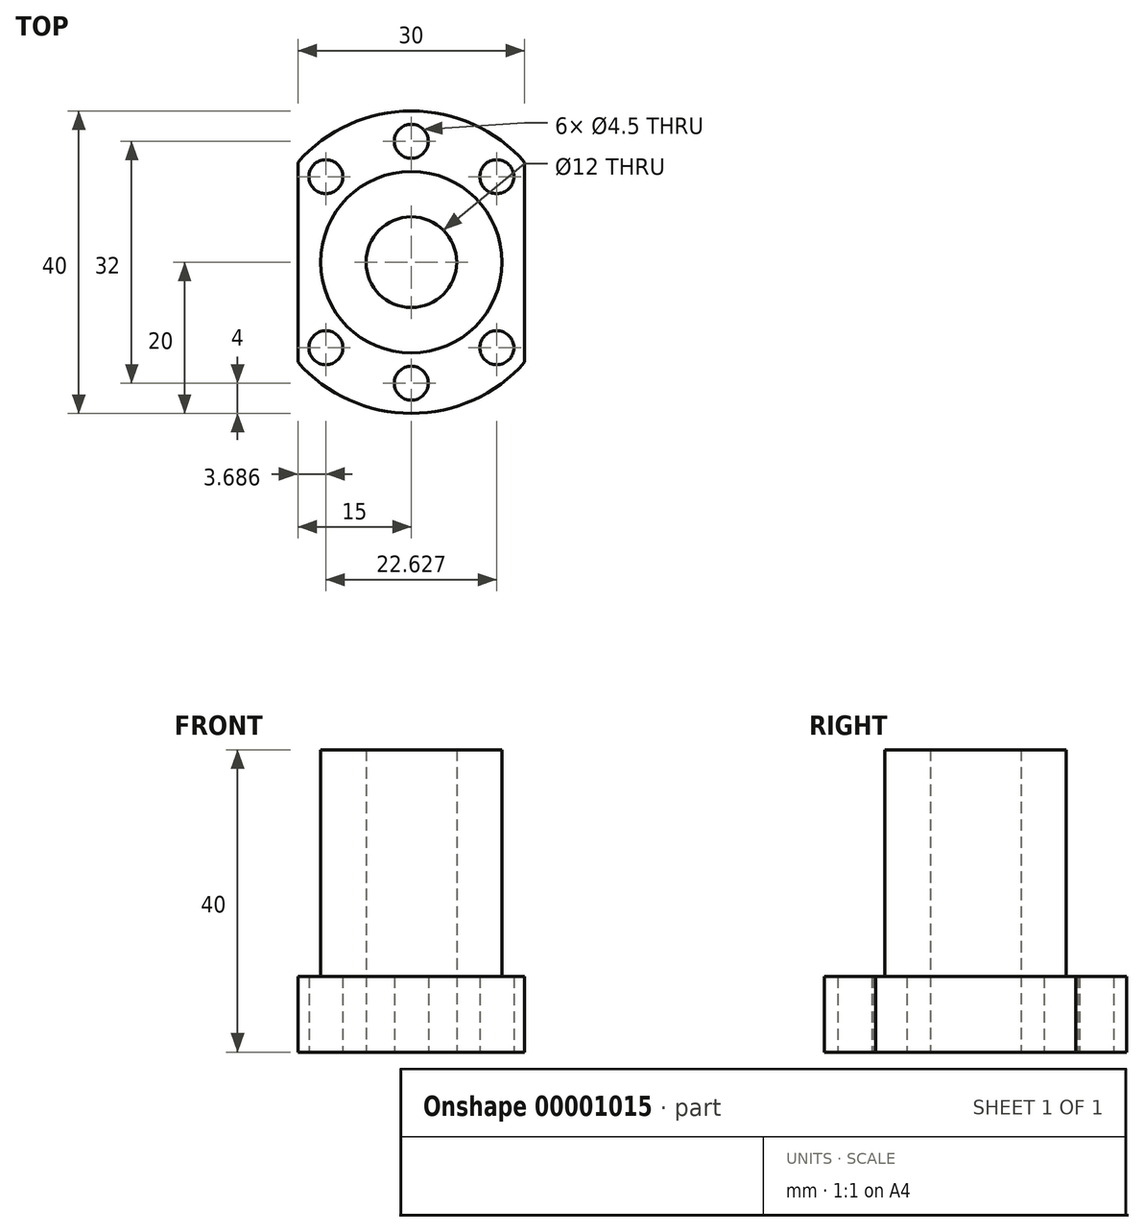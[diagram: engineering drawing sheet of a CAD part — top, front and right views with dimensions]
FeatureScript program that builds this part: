
annotation { "Feature Type Name" : "Feature", "Feature Type Description" : "" }
export const myFeature = defineFeature(function(context is Context, id is Id, definition is map)
    precondition{}
    {
        {
            var Q0;
            Q0=qCreatedBy(makeId("Top.planeOp"),FACE);
            var sketch = newSketch(context, id + "F0", { "sketchPlane" : qUnion([Q0])});
            skArc(sketch, "E0", {"start": v(-15, -13.23) * mm, "mid": v(0, -20) * mm, "end": v(15, -13.23) * mm});
            skLineSegment(sketch, "E1.rect.left", {"start": v(-15, 13.23) * mm, "end": v(-15, -13.23) * mm});
            skLineSegment(sketch, "E1.rect.right", {"start": v(15, 13.23) * mm, "end": v(15, -13.23) * mm});
            skPoint(sketch, "E1.rect.top.start.orphan", {"position": v(-15, -32.41) * mm});
            skPoint(sketch, "E2.orphan", {"position": v(15, -32.41) * mm});
            skArc(sketch, "E3.trimOffspring", {"start": v(15, 13.23) * mm, "mid": v(0, 20) * mm, "end": v(-15, 13.23) * mm});
            skPoint(sketch, "E1.rect.bottom.start.orphan", {"position": v(-15, 32.41) * mm});
            skPoint(sketch, "E4.orphan", {"position": v(15, 32.41) * mm});
            skCircle(sketch, "E5", {"center": v(0, 0) * mm, "radius": 16 * mm, "construction": true});
            skCircle(sketch, "E6", {"center": v(0, 0) * mm, "radius": 6 * mm});
            skCircle(sketch, "E7", {"center": v(0, 16) * mm, "radius": 2.25 * mm});
            skCircle(sketch, "E8", {"center": v(11.31, 11.31) * mm, "radius": 2.25 * mm});
            skCircle(sketch, "E9", {"center": v(-11.31, 11.31) * mm, "radius": 2.25 * mm});
            skLineSegment(sketch, "E10", {"start": v(0, 0) * mm, "end": v(-31.3, 0) * mm, "construction": true});
            skLineSegment(sketch, "E11", {"start": v(0, 0) * mm, "end": v(-29.04, 29.04) * mm, "construction": true});
            skLineSegment(sketch, "E12", {"start": v(0, 0) * mm, "end": v(25.68, 25.68) * mm, "construction": true});
            skCircle(sketch, "E13.0.MirrorC", {"center": v(11.31, -11.31) * mm, "radius": 2.25 * mm});
            skCircle(sketch, "E13.1.MirrorC", {"center": v(0, -16) * mm, "radius": 2.25 * mm});
            skCircle(sketch, "E13.2.MirrorC", {"center": v(-11.31, -11.31) * mm, "radius": 2.25 * mm});
            skSolve(sketch);
        }
        {
            var Q0;
            Q0=makeQuery(id+"F0.imprint","IMPRINT",FACE,{"disambiguationData":[TD([[makeQuery(id+"F0.imprint","IMPRINT",EDGE,{"derivedFrom":sQuery(id+"F0.wireOp",EDGE,"E0")}),1.0]])]});
            extrude(context, id + "F1", {"entities" : qUnion([Q0]), "depth" : 40 * mm});
        }
        {
            var Q0;
            Q0=makeQuery(id+"F1.opExtrude","CAP_FACE",FACE,{"disambiguationData":[OSD([sQuery(id+"F0.wireOp",EDGE,"E0"),sQuery(id+"F0.wireOp",EDGE,"E1.rect.left"),sQuery(id+"F0.wireOp",EDGE,"E1.rect.right"),sQuery(id+"F0.wireOp",EDGE,"E3.trimOffspring"),sQuery(id+"F0.wireOp",EDGE,"E6"),sQuery(id+"F0.wireOp",EDGE,"E7"),sQuery(id+"F0.wireOp",EDGE,"E8"),sQuery(id+"F0.wireOp",EDGE,"E9"),sQuery(id+"F0.wireOp",EDGE,"E13.0.MirrorC"),sQuery(id+"F0.wireOp",EDGE,"E13.1.MirrorC"),sQuery(id+"F0.wireOp",EDGE,"E13.2.MirrorC")])],"isStart":false});
            var sketch = newSketch(context, id + "F2", { "sketchPlane" : qUnion([Q0])});
            skCircle(sketch, "E14", {"center": v(0, 0) * mm, "radius": 12 * mm});
            skCircle(sketch, "E15", {"center": v(0, 0) * mm, "radius": 27.62 * mm});
            skSolve(sketch);
        }
        {
            var Q0;
            Q0=makeQuery(id+"F2.imprint","IMPRINT",FACE,{"disambiguationData":[TD([[makeQuery(id+"F2.imprint","IMPRINT",EDGE,{"derivedFrom":sQuery(id+"F2.wireOp",EDGE,"E15")}),1.0]])]});
            var Q1;
            Q1=makeQuery(id+"F2.imprint","IMPRINT",FACE,{"disambiguationData":[TD([[makeQuery(id+"F2.imprint","IMPRINT",EDGE,{"derivedFrom":makeQuery(id+"F1.opExtrude","CAP_EDGE",EDGE,{"disambiguationData":[OSD([sQuery(id+"F0.wireOp",EDGE,"E6")])],"isStart":false})}),1.0]])]});
            var Q2;
            Q2=makeQuery(id+"F2.imprint","IMPRINT",FACE,{"disambiguationData":[TD([[makeQuery(id+"F2.imprint","IMPRINT",EDGE,{"derivedFrom":makeQuery(id+"F1.opExtrude","CAP_EDGE",EDGE,{"disambiguationData":[OSD([sQuery(id+"F0.wireOp",EDGE,"E7")])],"isStart":false})}),1.0]])]});
            var Q3;
            Q3=makeQuery(id+"F2.imprint","IMPRINT",FACE,{"disambiguationData":[TD([[makeQuery(id+"F2.imprint","IMPRINT",EDGE,{"derivedFrom":makeQuery(id+"F1.opExtrude","CAP_EDGE",EDGE,{"disambiguationData":[OSD([sQuery(id+"F0.wireOp",EDGE,"E8")])],"isStart":false})}),1.0]])]});
            var Q4;
            Q4=makeQuery(id+"F2.imprint","IMPRINT",FACE,{"disambiguationData":[TD([[makeQuery(id+"F2.imprint","IMPRINT",EDGE,{"derivedFrom":makeQuery(id+"F1.opExtrude","CAP_EDGE",EDGE,{"disambiguationData":[OSD([sQuery(id+"F0.wireOp",EDGE,"E9")])],"isStart":false})}),1.0]])]});
            var Q5;
            Q5=makeQuery(id+"F2.imprint","IMPRINT",FACE,{"disambiguationData":[TD([[makeQuery(id+"F2.imprint","IMPRINT",EDGE,{"derivedFrom":makeQuery(id+"F1.opExtrude","CAP_EDGE",EDGE,{"disambiguationData":[OSD([sQuery(id+"F0.wireOp",EDGE,"E13.0.MirrorC")])],"isStart":false})}),-1.0]])]});
            var Q6;
            Q6=makeQuery(id+"F2.imprint","IMPRINT",FACE,{"disambiguationData":[TD([[makeQuery(id+"F2.imprint","IMPRINT",EDGE,{"derivedFrom":makeQuery(id+"F1.opExtrude","CAP_EDGE",EDGE,{"disambiguationData":[OSD([sQuery(id+"F0.wireOp",EDGE,"E13.1.MirrorC")])],"isStart":false})}),-1.0]])]});
            var Q7;
            Q7=makeQuery(id+"F2.imprint","IMPRINT",FACE,{"disambiguationData":[TD([[makeQuery(id+"F2.imprint","IMPRINT",EDGE,{"derivedFrom":makeQuery(id+"F1.opExtrude","CAP_EDGE",EDGE,{"disambiguationData":[OSD([sQuery(id+"F0.wireOp",EDGE,"E13.2.MirrorC")])],"isStart":false})}),-1.0]])]});
            var Q8;
            Q8=makeQuery(id+"F2.imprint","IMPRINT",FACE,{"disambiguationData":[TD([[makeQuery(id+"F2.imprint","IMPRINT",EDGE,{"derivedFrom":sQuery(id+"F2.wireOp",EDGE,"E14")}),-1.0]])]});
            extrude(context, id + "F3", {"entities" : qUnion([Q0, Q1, Q2, Q3, Q4, Q5, Q6, Q7, Q8]), "operationType" : NewBodyOperationType.REMOVE, "oppositeDirection" : true, "depth" : 30 * mm});
        }
    });
